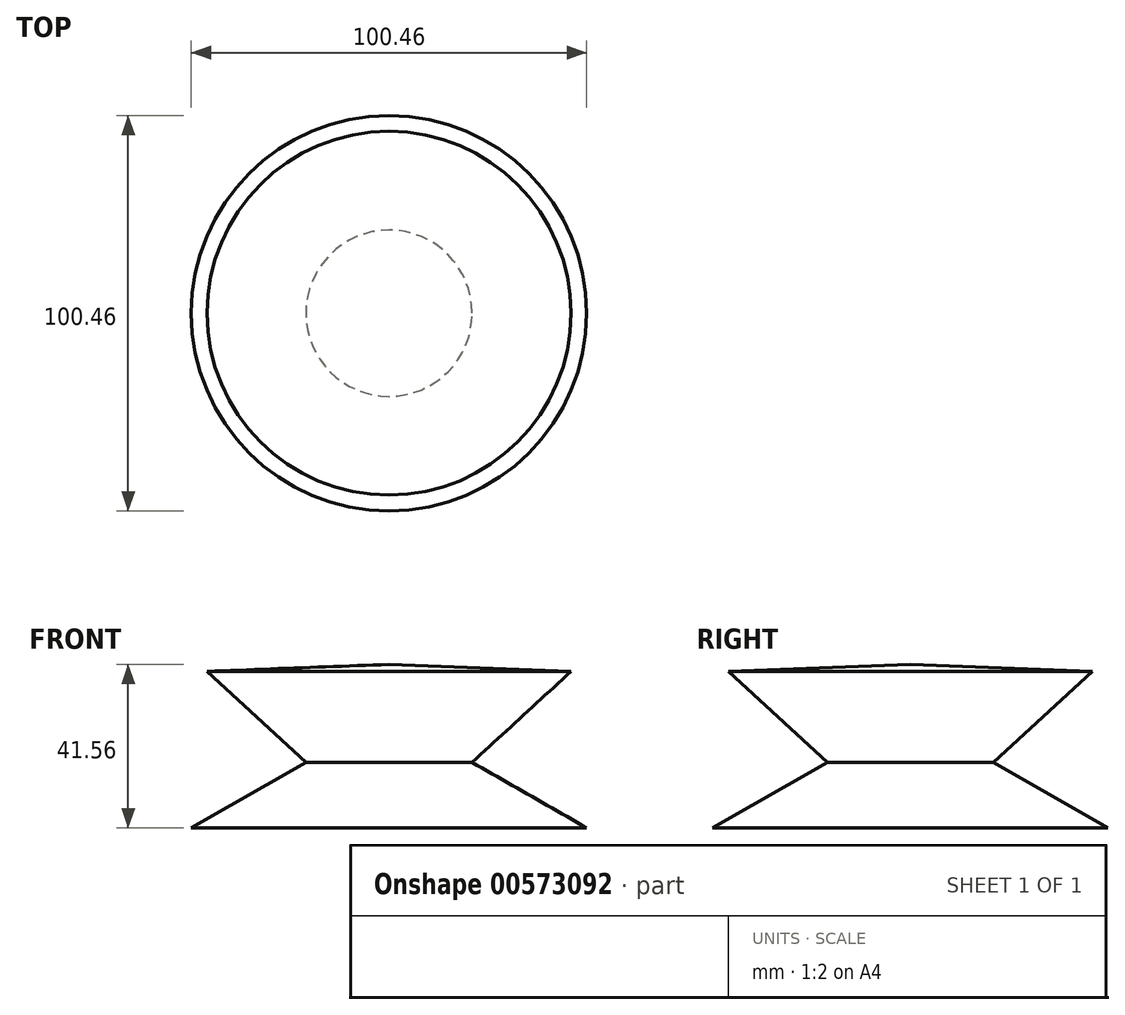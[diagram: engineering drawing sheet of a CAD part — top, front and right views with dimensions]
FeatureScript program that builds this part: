
annotation { "Feature Type Name" : "Feature", "Feature Type Description" : "" }
export const myFeature = defineFeature(function(context is Context, id is Id, definition is map)
    precondition{}
    {
        {
            var Q0;
            Q0=qCreatedBy(makeId("Front.planeOp"),FACE);
            var sketch = newSketch(context, id + "F0", { "sketchPlane" : qUnion([Q0])});
            skLineSegment(sketch, "E0", {"start": v(0, 0) * mm, "end": v(-50.23, 0) * mm});
            skLineSegment(sketch, "E1", {"start": v(-50.23, 0) * mm, "end": v(-21.11, 16.67) * mm});
            skLineSegment(sketch, "E2", {"start": v(-21.11, 16.67) * mm, "end": v(-46.23, 39.78) * mm});
            skLineSegment(sketch, "E3", {"start": v(-46.23, 39.78) * mm, "end": v(0, 41.56) * mm});
            skLineSegment(sketch, "E4", {"start": v(0, 41.56) * mm, "end": v(0, 0) * mm});
            skSolve(sketch);
        }
        {
            var Q0;
            Q0=makeQuery(id+"F0.imprint","IMPRINT",FACE,{"disambiguationData":[TD([[makeQuery(id+"F0.imprint","IMPRINT",EDGE,{"derivedFrom":sQuery(id+"F0.wireOp",EDGE,"E0")}),-1.0]])]});
            var Q1;
            Q1=sQuery(id+"F0.wireOp",EDGE,"E4");
            revolve(context, id + "F1", {"entities" : qUnion([Q0]), "axis" : qUnion([Q1]), "revolveType" : RevolveType.FULL});
        }
    });
